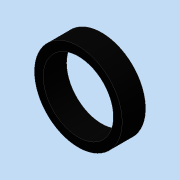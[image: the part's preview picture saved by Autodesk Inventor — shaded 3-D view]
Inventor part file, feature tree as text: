
AUTODESK INVENTOR PART (.ipt)
format: ipt  version: 2016 (Build 200138000, 138)  size: 93,696 bytes
history: native  units: mm
features: extrude x1, sketch x1
ambient origin geometry x8: Origin, YZ Plane, XZ Plane, XY Plane, X Axis, Y Axis, Z Axis, Center Point
bodies: Solid1 (feature_tree)
feature tree (2):
  extrude  "Extrusion1"  Depth=2.0mm
  sketch  "Sketch1"  dims[d0=7.5mm d1=6.0mm d2=2.0mm d3=0.0mm]
